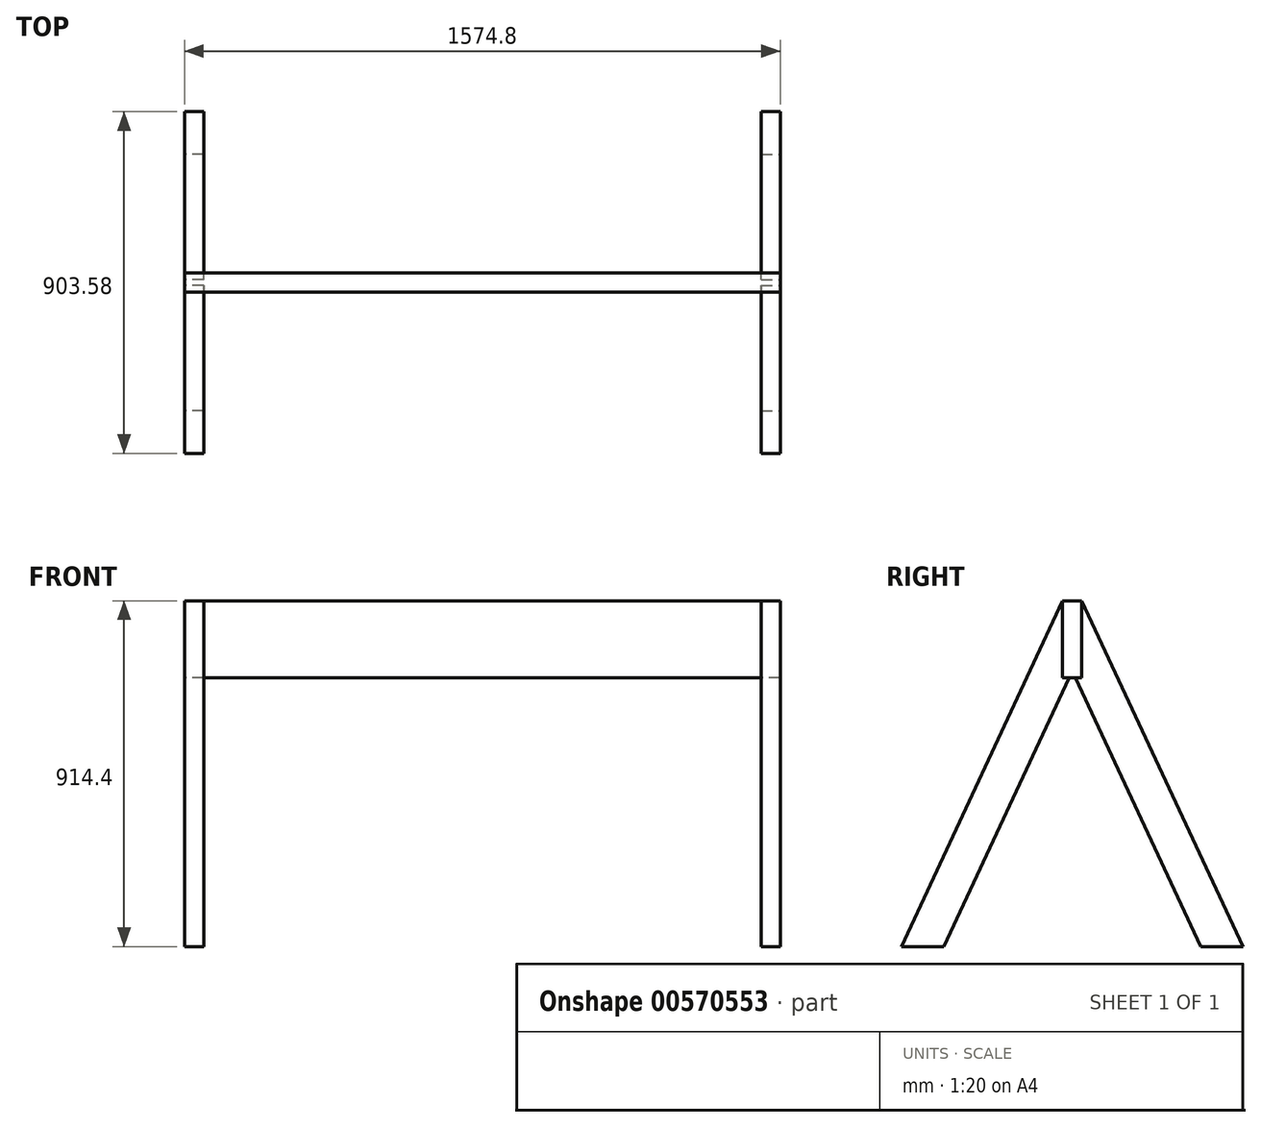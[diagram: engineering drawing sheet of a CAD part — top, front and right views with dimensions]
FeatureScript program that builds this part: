
annotation { "Feature Type Name" : "Feature", "Feature Type Description" : "" }
export const myFeature = defineFeature(function(context is Context, id is Id, definition is map)
    precondition{}
    {
        {
            var Q0;
            Q0=qCreatedBy(makeId("Front.planeOp"),FACE);
            var sketch = newSketch(context, id + "F0", { "sketchPlane" : qUnion([Q0])});
            skLineSegment(sketch, "E0.bottom", {"start": v(0, 101.6) * mm, "end": v(787.4, 101.6) * mm});
            skLineSegment(sketch, "E0.top", {"start": v(0, -101.6) * mm, "end": v(787.4, -101.6) * mm});
            skLineSegment(sketch, "E0.left", {"start": v(0, 101.6) * mm, "end": v(0, -101.6) * mm});
            skLineSegment(sketch, "E0.right", {"start": v(787.4, 101.6) * mm, "end": v(787.4, -101.6) * mm});
            skLineSegment(sketch, "E1", {"start": v(0, 0) * mm, "end": v(787.4, 0) * mm, "construction": true});
            skSolve(sketch);
        }
        {
            var Q0;
            Q0 = qSketchRegion(id + "F0", true);
            extrude(context, id + "F1", {"entities" : qUnion([Q0]), "endBound" : BoundingType.SYMMETRIC, "depth" : 50.8 * mm, "offsetDistance" : 25.4 * mm});
        }
        {
            var Q0;
            Q0=makeQuery(id+"F1.opExtrude","SWEPT_FACE",FACE,{"disambiguationData":[OSD([sQuery(id+"F0.wireOp",EDGE,"E0.right")])]});
            var sketch = newSketch(context, id + "F2", { "sketchPlane" : qUnion([Q0])});
            skLineSegment(sketch, "E2", {"start": v(-8.05, -101.6) * mm, "end": v(-339.69, -812.8) * mm});
            skLineSegment(sketch, "E3", {"start": v(-25.4, 101.6) * mm, "end": v(-451.8, -812.8) * mm});
            skLineSegment(sketch, "E4", {"start": v(-451.8, -812.8) * mm, "end": v(-339.69, -812.8) * mm});
            skLineSegment(sketch, "E5", {"start": v(0, 0) * mm, "end": v(0, -812.8) * mm, "construction": true});
            skLineSegment(sketch, "E6", {"start": v(-25.4, 101.6) * mm, "end": v(-25.4, -101.6) * mm});
            skLineSegment(sketch, "E7", {"start": v(-25.4, -101.6) * mm, "end": v(-8.05, -101.6) * mm});
            skLineSegment(sketch, "E8.MirrorCS", {"start": v(25.4, -101.6) * mm, "end": v(8.05, -101.6) * mm});
            skLineSegment(sketch, "E9.MirrorCS", {"start": v(451.8, -812.8) * mm, "end": v(339.69, -812.8) * mm});
            skLineSegment(sketch, "E10.MirrorCS", {"start": v(25.4, 101.6) * mm, "end": v(25.4, -101.6) * mm});
            skLineSegment(sketch, "E11.MirrorCS", {"start": v(8.05, -101.6) * mm, "end": v(339.69, -812.8) * mm});
            skLineSegment(sketch, "E12.MirrorCS", {"start": v(25.4, 101.6) * mm, "end": v(451.8, -812.8) * mm});
            skSolve(sketch);
        }
        {
            var Q0;
            Q0 = qSketchRegion(id + "F2", true);
            extrude(context, id + "F3", {"entities" : qUnion([Q0]), "oppositeDirection" : true, "depth" : 50.8 * mm, "offsetDistance" : 25.4 * mm});
        }
        {
            var Q0;
            Q0=makeQuery(id+"F1.opExtrude","SWEPT_BODY",BODY,{"disambiguationData":[OSD([sQuery(id+"F0.wireOp",EDGE,"E0.bottom"),sQuery(id+"F0.wireOp",EDGE,"E0.top"),sQuery(id+"F0.wireOp",EDGE,"E0.left"),sQuery(id+"F0.wireOp",EDGE,"E0.right")])]});
            var Q1;
            Q1=qCreatedBy(makeId("Right.planeOp"),FACE);
            mirror(context, id + "F4", {"operationType" : NewBodyOperationType.ADD, "entities" : qUnion([Q0]), "mirrorPlane" : qUnion([Q1])});
        }
        {
            var Q0;
            Q0=makeQuery(id+"F3.opExtrude","SWEPT_BODY",BODY,{"disambiguationData":[OSD([sQuery(id+"F2.wireOp",EDGE,"E2"),sQuery(id+"F2.wireOp",EDGE,"E3"),sQuery(id+"F2.wireOp",EDGE,"E4"),sQuery(id+"F2.wireOp",EDGE,"E6"),sQuery(id+"F2.wireOp",EDGE,"E7")])]});
            var Q1;
            Q1=makeQuery(id+"F3.opExtrude","SWEPT_BODY",BODY,{"disambiguationData":[OSD([sQuery(id+"F2.wireOp",EDGE,"E8.MirrorCS"),sQuery(id+"F2.wireOp",EDGE,"E9.MirrorCS"),sQuery(id+"F2.wireOp",EDGE,"E10.MirrorCS"),sQuery(id+"F2.wireOp",EDGE,"E11.MirrorCS"),sQuery(id+"F2.wireOp",EDGE,"E12.MirrorCS")])]});
            var Q2;
            Q2=qCreatedBy(makeId("Right.planeOp"),FACE);
            mirror(context, id + "F5", {"entities" : qUnion([Q0, Q1]), "mirrorPlane" : qUnion([Q2])});
        }
    });
